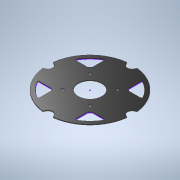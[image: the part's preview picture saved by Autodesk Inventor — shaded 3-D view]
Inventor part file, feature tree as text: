
AUTODESK INVENTOR PART (.ipt)
format: ipt  version: 2020 (Build 240168000, 168)  size: 218,624 bytes
history: native  units: mm
features: sketch x4, extrude x2, other x1, fillet x1
ambient origin geometry x8: Origin, YZ Plane, XZ Plane, XY Plane, X Axis, Y Axis, Z Axis, Center Point
bodies: Body1 (feature_tree)
feature tree (8):
  other  "Твердое тело1"
  sketch  "Эскиз1"
  sketch  "Эскиз4"
  extrude  "Выдавливание1"  Depth=8.0mm
  fillet  "Сопряжение1"  Radius=40.0mm
  extrude  "Выдавливание2"  Depth=112.2mm
  sketch  "Эскиз2"
  sketch  "Эскиз5"
